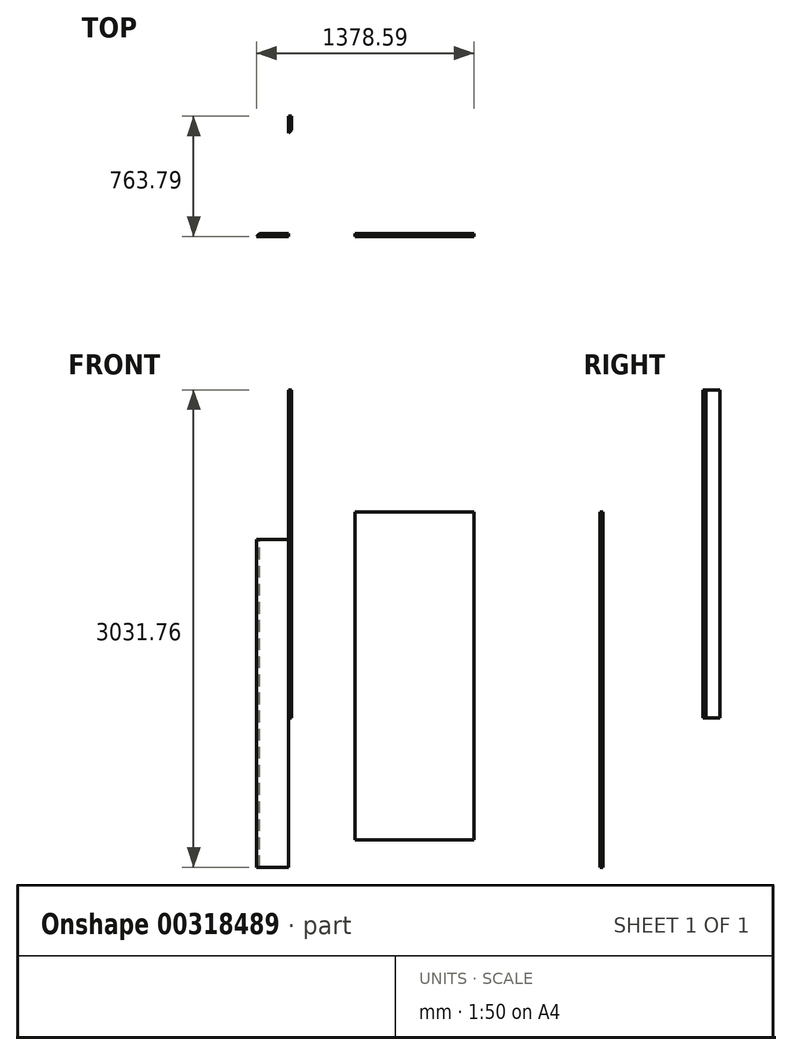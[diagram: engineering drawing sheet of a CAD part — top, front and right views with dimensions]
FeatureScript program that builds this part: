
annotation { "Feature Type Name" : "Feature", "Feature Type Description" : "" }
export const myFeature = defineFeature(function(context is Context, id is Id, definition is map)
    precondition{}
    {
        {
            var Q0;
            Q0=qCreatedBy(makeId("Front.planeOp"),FACE);
            var sketch = newSketch(context, id + "F0", { "sketchPlane" : qUnion([Q0])});
            skLineSegment(sketch, "E0.bottom", {"start": v(-203.2, 1721.8) * mm, "end": v(0, 1721.8) * mm});
            skLineSegment(sketch, "E0.top", {"start": v(-203.2, -361) * mm, "end": v(0, -361) * mm});
            skLineSegment(sketch, "E0.left", {"start": v(-203.2, 1721.8) * mm, "end": v(-203.2, -361) * mm});
            skLineSegment(sketch, "E0.right", {"start": v(0, 1721.8) * mm, "end": v(0, -361) * mm});
            skSolve(sketch);
        }
        {
            var Q0;
            Q0 = qSketchRegion(id + "F0", true);
            extrude(context, id + "F1", {"entities" : qUnion([Q0]), "depth" : 19.05 * mm});
        }
        {
            var Q0;
            Q0=makeQuery(id+"F1.opExtrude","SWEPT_FACE",FACE,{"disambiguationData":[OSD([sQuery(id+"F0.wireOp",EDGE,"E0.bottom")])]});
            var sketch = newSketch(context, id + "F2", { "sketchPlane" : qUnion([Q0])});
            skLineSegment(sketch, "E1.0", {"start": v(-184.15, -19.05) * mm, "end": v(-184.15, 0) * mm, "construction": true});
            skLineSegment(sketch, "E2", {"start": v(-203.2, -19.05) * mm, "end": v(-184.15, 0) * mm});
            skSolve(sketch);
        }
        {
            var Q0;
            {var subQ0=sQuery(id+"F2.wireOp",EDGE,"E2");Q0=makeQuery(id+"F2.imprint","IMPRINT",FACE,{"disambiguationData":[TD([[makeQuery(id+"F2.imprint","IMPRINT",EDGE,{"derivedFrom":subQ0}),1.0]])]});}
            extrude(context, id + "F3", {"entities" : qUnion([Q0]), "operationType" : NewBodyOperationType.REMOVE, "oppositeDirection" : true, "depth" : 2082.8 * mm});
        }
        {
            var Q0;
            Q0=qCreatedBy(makeId("Front.planeOp"),FACE);
            var sketch = newSketch(context, id + "F4", { "sketchPlane" : qUnion([Q0])});
            skLineSegment(sketch, "E3.bottom", {"start": v(419.74, 1897.16) * mm, "end": v(1175.4, 1897.16) * mm});
            skLineSegment(sketch, "E3.top", {"start": v(419.74, -185.64) * mm, "end": v(1175.4, -185.64) * mm});
            skLineSegment(sketch, "E3.left", {"start": v(419.74, 1897.16) * mm, "end": v(419.74, -185.64) * mm});
            skLineSegment(sketch, "E3.right", {"start": v(1175.4, 1897.16) * mm, "end": v(1175.4, -185.64) * mm});
            skSolve(sketch);
        }
        {
            var Q0;
            Q0 = qSketchRegion(id + "F4", true);
            extrude(context, id + "F5", {"entities" : qUnion([Q0]), "depth" : 19.05 * mm});
        }
        {
            var Q0;
            Q0=qCreatedBy(makeId("Right.planeOp"),FACE);
            var sketch = newSketch(context, id + "F6", { "sketchPlane" : qUnion([Q0])});
            skLineSegment(sketch, "E4.bottom", {"start": v(744.74, 2670.76) * mm, "end": v(636.79, 2670.76) * mm});
            skLineSegment(sketch, "E4.top", {"start": v(744.74, 587.96) * mm, "end": v(636.79, 587.96) * mm});
            skLineSegment(sketch, "E4.left", {"start": v(744.74, 2670.76) * mm, "end": v(744.74, 587.96) * mm});
            skLineSegment(sketch, "E4.right", {"start": v(636.79, 2670.76) * mm, "end": v(636.79, 587.96) * mm});
            skSolve(sketch);
        }
        {
            var Q0;
            Q0 = qSketchRegion(id + "F6", true);
            extrude(context, id + "F7", {"entities" : qUnion([Q0]), "depth" : 19.05 * mm});
        }
        {
            var Q0;
            Q0=makeQuery(id+"F7.opExtrude","SWEPT_FACE",FACE,{"disambiguationData":[OSD([sQuery(id+"F6.wireOp",EDGE,"E4.bottom")])]});
            var sketch = newSketch(context, id + "F8", { "sketchPlane" : qUnion([Q0])});
            skLineSegment(sketch, "E5.0", {"start": v(19.05, 655.84) * mm, "end": v(0, 655.84) * mm, "construction": true});
            skLineSegment(sketch, "E6", {"start": v(19.05, 655.84) * mm, "end": v(0, 636.79) * mm});
            skSolve(sketch);
        }
        {
            var Q0;
            {var subQ0=sQuery(id+"F8.wireOp",EDGE,"E6");Q0=makeQuery(id+"F8.imprint","IMPRINT",FACE,{"disambiguationData":[TD([[makeQuery(id+"F8.imprint","IMPRINT",EDGE,{"derivedFrom":subQ0}),1.0]])]});}
            extrude(context, id + "F9", {"entities" : qUnion([Q0]), "operationType" : NewBodyOperationType.REMOVE, "oppositeDirection" : true, "depth" : 2082.8 * mm});
        }
    });
